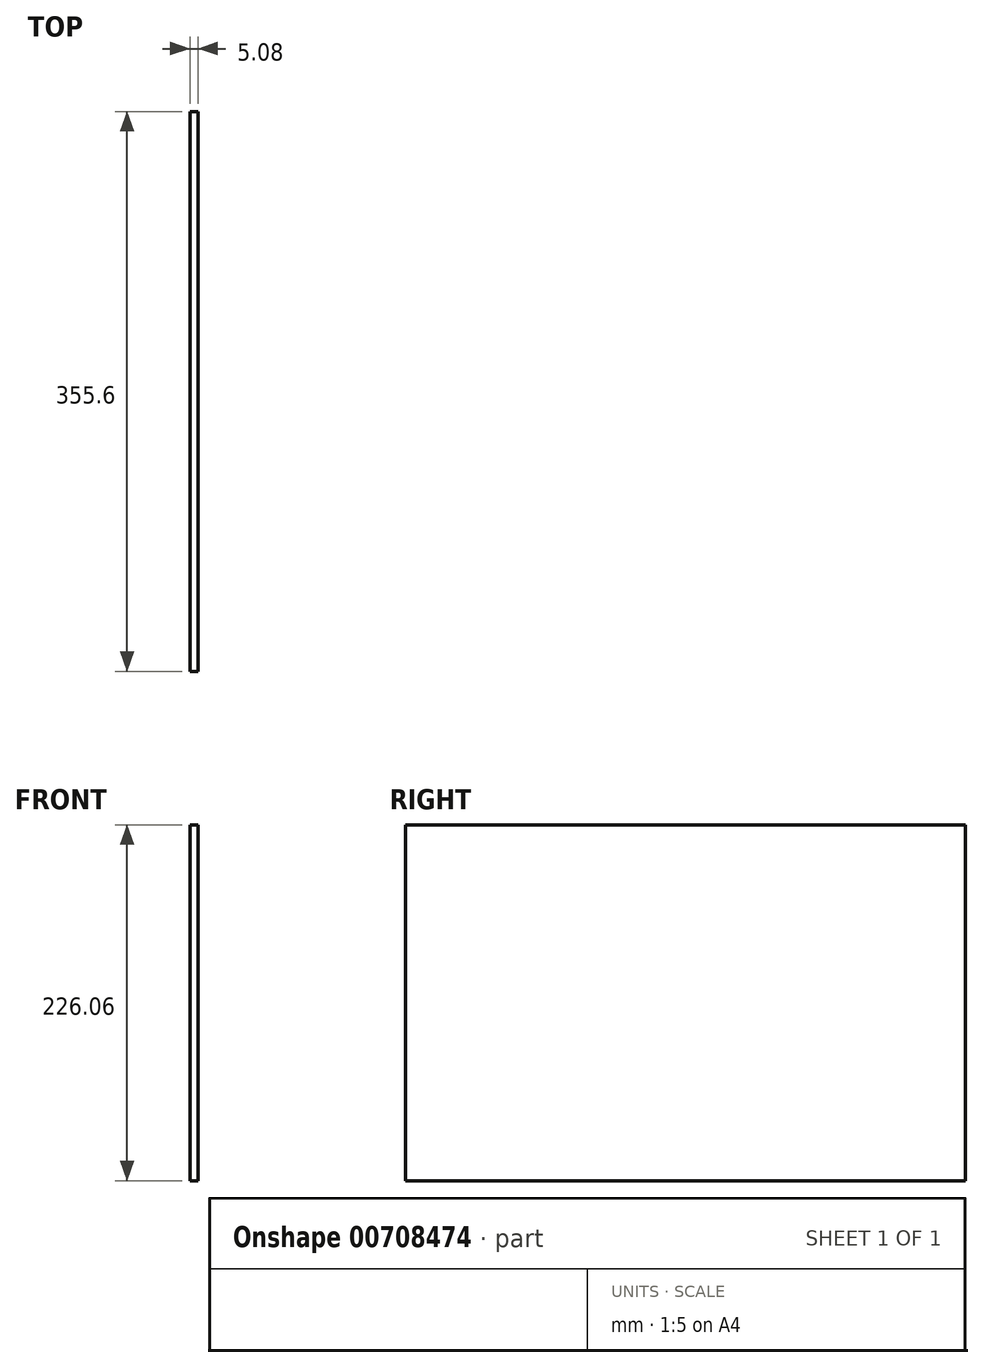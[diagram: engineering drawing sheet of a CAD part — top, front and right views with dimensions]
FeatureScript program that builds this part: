
annotation { "Feature Type Name" : "Feature", "Feature Type Description" : "" }
export const myFeature = defineFeature(function(context is Context, id is Id, definition is map)
    precondition{}
    {
        {
            var Q0;
            Q0=qCreatedBy(makeId("Front.planeOp"),FACE);
            var sketch = newSketch(context, id + "F0", { "sketchPlane" : qUnion([Q0])});
            skLineSegment(sketch, "E0.bottom", {"start": v(0, 0) * mm, "end": v(-5.08, 0) * mm});
            skLineSegment(sketch, "E0.top", {"start": v(0, -226.06) * mm, "end": v(-5.08, -226.06) * mm});
            skLineSegment(sketch, "E0.left", {"start": v(0, 0) * mm, "end": v(0, -226.06) * mm});
            skLineSegment(sketch, "E0.right", {"start": v(-5.08, 0) * mm, "end": v(-5.08, -226.06) * mm});
            skSolve(sketch);
        }
        {
            var Q0;
            Q0 = qSketchRegion(id + "F0", true);
            extrude(context, id + "F1", {"entities" : qUnion([Q0]), "depth" : 355.6 * mm, "offsetDistance" : 25.4 * mm});
        }
    });
